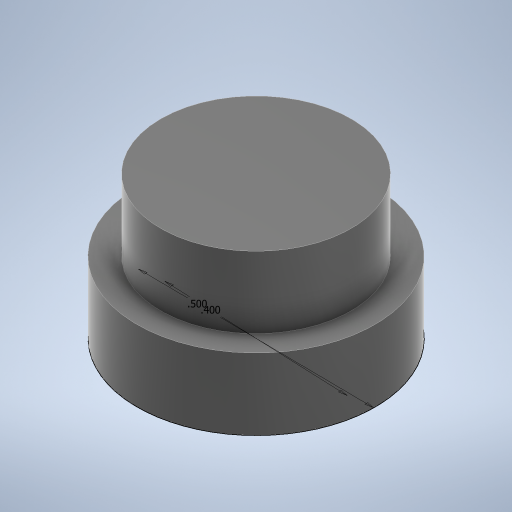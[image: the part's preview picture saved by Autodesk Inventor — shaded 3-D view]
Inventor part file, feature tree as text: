
AUTODESK INVENTOR PART (.ipt)
format: ipt  version: 2023 (Build 270158000, 158)  size: 226,816 bytes
history: native  units: in
note: dims shown in document units (in); Inventor stores cm internally (conversion verified against a paired STEP export)
features: extrude x2, sketch x1
ambient origin geometry x8: Origin, YZ Plane, XZ Plane, XY Plane, X Axis, Y Axis, Z Axis, Center Point
bodies: Solid1 (feature_tree)
feature tree (3):
  sketch  "Sketch1"  dims[d0=0.4in d1=0.5in d2=0.3in d3=0.0in d4=0.15in d5=0.0in]
  extrude  "Extrusion1"  Depth=0.15in
  extrude  "Extrusion2"  Depth=0.3in TaperAngle=0.0deg
